# Revit family: Sanitary_Showers_hansgrohe_24531CHN-Raindance-Alive-Q-Overhead-shower-210-340-1jet_new
name_source: partatom
category: Plumbing Fixtures
units: mm (PartAtom-declared; Revit-internal decimal feet)

## family parameters
Always vertical = No
Cut with Voids When Loaded = No
Maintain Annotation Orientation = No
OmniClass Number = 23.31.17.00
OmniClass Title = Showers
Part Type = Normal
Room Calculation Point = No
Round Connector Dimension = Use Diameter
Shared = No
Work Plane-Based = Yes

## types (4) — shared parameters
Connector Description = Water Inlet 12.7 mm
Default Elevation = 1219 mm
Description = Raindance Alive Q Overhead shower 210/340 1jet
Diameter = 13 mm
Manufacturer = Hansgrohe
Material 2 = Hansgrohe - Plastic - Graphite
Model = 24531CHN
Product Page URL = https://www.hansgrohe.com
Product data url = https://bimobject.com
URL = https://www.hansgrohe.com
Version = 1

## per-type parameters (varying)
| type | Material 1 |
| 007 Chrome | Hansgrohe - Metal - 007 Chrome |
| 677 Matte Black | Hansgrohe - Metal - 677 Matte Black |
| 707 Matte White | Hansgrohe - Metal - 707 Matte White |
| 997 Polished Gold Optic | Hansgrohe - Metal - 997 Polished Gold Optic |

## geometry (parser evidence)
native form markers: Sweep x3
no freeform markers — native parametric forms only
